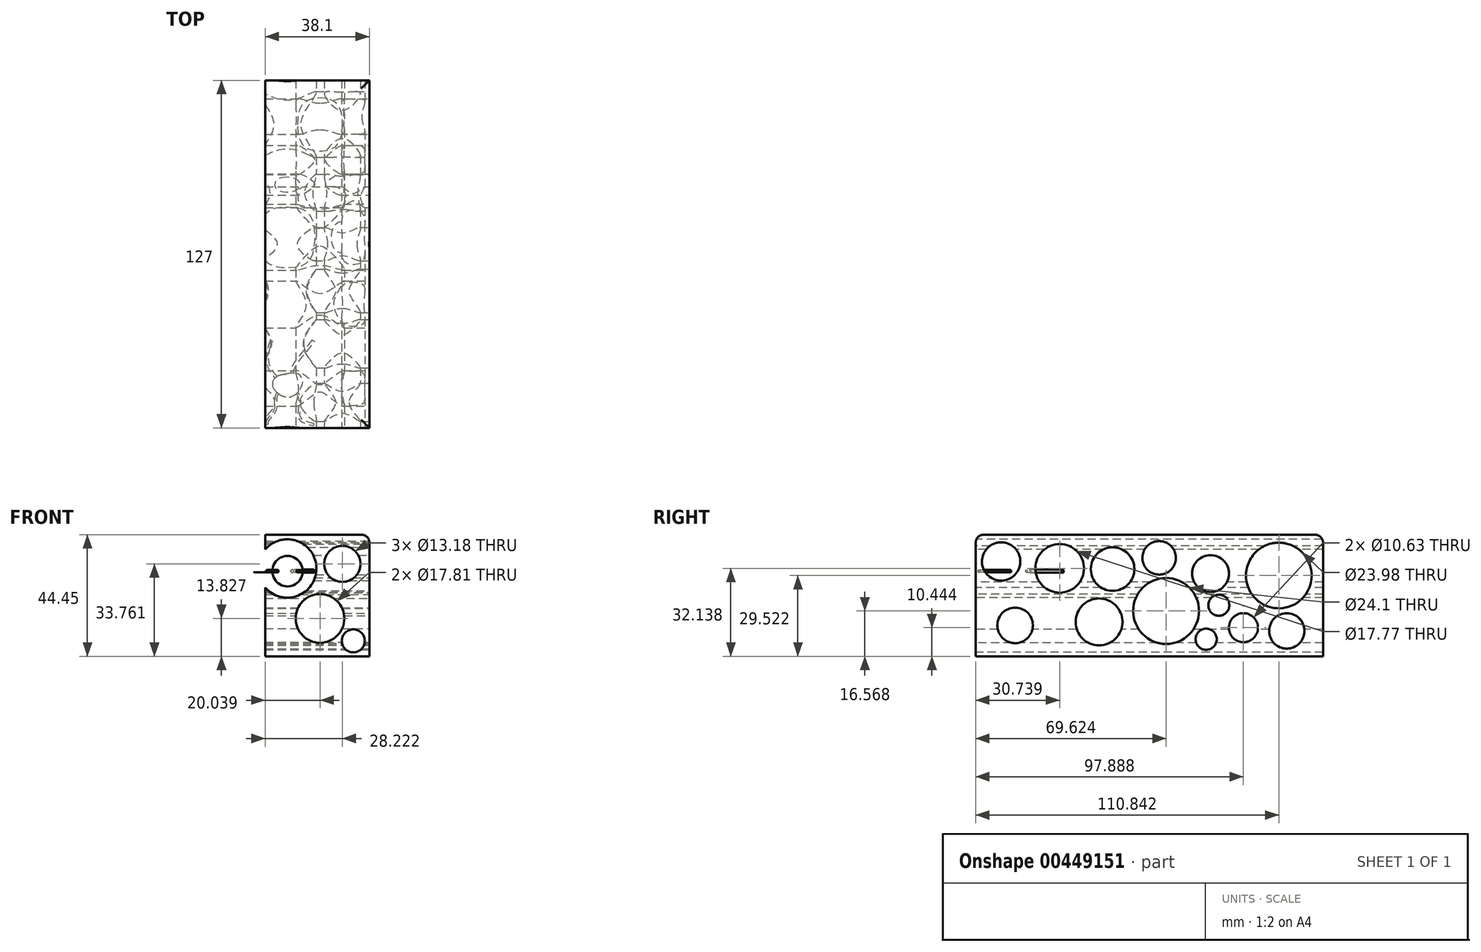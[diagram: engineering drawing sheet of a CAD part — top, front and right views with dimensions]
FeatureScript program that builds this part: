
annotation { "Feature Type Name" : "Feature", "Feature Type Description" : "" }
export const myFeature = defineFeature(function(context is Context, id is Id, definition is map)
    precondition{}
    {
        {
            var Q0;
            Q0=qCreatedBy(makeId("Front.planeOp"),FACE);
            var sketch = newSketch(context, id + "F0", { "sketchPlane" : qUnion([Q0])});
            skLineSegment(sketch, "E0.bottom", {"start": v(-47.65, 23.5) * mm, "end": v(53.95, 23.5) * mm});
            skLineSegment(sketch, "E0.top", {"start": v(-47.65, -20.95) * mm, "end": v(53.95, -20.95) * mm});
            skLineSegment(sketch, "E0.left", {"start": v(-47.65, 23.5) * mm, "end": v(-47.65, -20.95) * mm});
            skLineSegment(sketch, "E0.right", {"start": v(53.95, 23.5) * mm, "end": v(53.95, -20.95) * mm});
            skSolve(sketch);
        }
        {
            var Q0;
            Q0=qSketchRegion(id+"F0",true);
            extrude(context, id + "F1", {"entities" : qUnion([Q0]), "endBound" : BoundingType.SYMMETRIC, "depth" : 127 * mm});
        }
        {
            var Q0;
            Q0=makeQuery(id+"F1.opExtrude","SWEPT_FACE",FACE,{"disambiguationData":[OSD([sQuery(id+"F0.wireOp",EDGE,"E0.right")])]});
            var sketch = newSketch(context, id + "F2", { "sketchPlane" : qUnion([Q0])});
            skCircle(sketch, "E1", {"center": v(-13.43, 10.93) * mm, "radius": 7.97 * mm});
            skCircle(sketch, "E2", {"center": v(6.12, -4.38) * mm, "radius": 12.05 * mm});
            skCircle(sketch, "E3", {"center": v(47.34, 8.57) * mm, "radius": 12 * mm});
            skCircle(sketch, "E4", {"center": v(34.39, -10.5) * mm, "radius": 5.31 * mm});
            skCircle(sketch, "E5", {"center": v(-32.76, 11.19) * mm, "radius": 8.88 * mm});
            skCircle(sketch, "E6", {"center": v(-18.37, -8.39) * mm, "radius": 8.57 * mm});
            skCircle(sketch, "E7", {"center": v(3.6, 15.02) * mm, "radius": 6.12 * mm});
            skCircle(sketch, "E8", {"center": v(22.38, 9.28) * mm, "radius": 6.74 * mm});
            skCircle(sketch, "E9", {"center": v(-49.06, -9.65) * mm, "radius": 6.5 * mm});
            skCircle(sketch, "E10", {"center": v(-54.17, 13.7) * mm, "radius": 7.01 * mm});
            skCircle(sketch, "E11", {"center": v(50.25, -11.68) * mm, "radius": 6.46 * mm});
            skCircle(sketch, "E12", {"center": v(20.78, -14.72) * mm, "radius": 3.87 * mm});
            skCircle(sketch, "E13", {"center": v(25.4, -2.3) * mm, "radius": 3.85 * mm});
            skSolve(sketch);
        }
        {
            var Q0;
            Q0=qSketchRegion(id+"F2",true);
            extrude(context, id + "F3", {"entities" : qUnion([Q0]), "operationType" : NewBodyOperationType.REMOVE, "endBound" : BoundingType.THROUGH_ALL, "oppositeDirection" : true, "depth" : 25.4 * mm});
        }
        {
            var Q0;
            Q0=makeQuery(id+"F1.opExtrude","CAP_FACE",FACE,{"disambiguationData":[OSD([sQuery(id+"F0.wireOp",EDGE,"E0.bottom"),sQuery(id+"F0.wireOp",EDGE,"E0.top"),sQuery(id+"F0.wireOp",EDGE,"E0.left"),sQuery(id+"F0.wireOp",EDGE,"E0.right")])],"isStart":false});
            var sketch = newSketch(context, id + "F4", { "sketchPlane" : qUnion([Q0])});
            skCircle(sketch, "E14", {"center": v(-37.55, 12.4) * mm, "radius": 8.73 * mm});
            skCircle(sketch, "E15", {"center": v(-15.94, 7.15) * mm, "radius": 11.37 * mm});
            skCircle(sketch, "E16", {"center": v(-35.46, -10.9) * mm, "radius": 9.74 * mm});
            skCircle(sketch, "E17", {"center": v(-16.15, -8.8) * mm, "radius": 3.78 * mm});
            skCircle(sketch, "E18", {"center": v(-3.56, -12.79) * mm, "radius": 7.5 * mm});
            skCircle(sketch, "E19", {"center": v(23.93, 11.13) * mm, "radius": 10.66 * mm});
            skCircle(sketch, "E20", {"center": v(35.89, -7.12) * mm, "radius": 8.9 * mm});
            skCircle(sketch, "E21", {"center": v(44.07, 12.81) * mm, "radius": 6.59 * mm});
            skCircle(sketch, "E22", {"center": v(48.06, -15.3) * mm, "radius": 4.2 * mm});
            skSolve(sketch);
        }
        {
            var Q0;
            Q0=qSketchRegion(id+"F4",true);
            extrude(context, id + "F5", {"entities" : qUnion([Q0]), "operationType" : NewBodyOperationType.REMOVE, "endBound" : BoundingType.THROUGH_ALL, "oppositeDirection" : true, "depth" : 25.4 * mm});
        }
        {
            var Q0;
            Q0=makeQuery(id+"F1.opExtrude","SWEPT_FACE",FACE,{"disambiguationData":[OSD([sQuery(id+"F0.wireOp",EDGE,"E0.left")])]});
            extrude(context, id + "F6", {"entities" : qUnion([Q0]), "operationType" : NewBodyOperationType.REMOVE, "oppositeDirection" : true, "depth" : 63.5 * mm});
        }
        {
            var Q0;
            Q0=qCreatedBy(makeId("Top.planeOp"),FACE);
            cPlane(context, id + "F7", {"entities" : qUnion([Q0]), "cplaneType" : CPlaneType.OFFSET, "offset" : 10.16 * mm, "width" : 152.4 * mm, "height" : 152.4 * mm});
        }
        {
            var Q0;
            Q0=qCreatedBy(id+"F7.planeOp",FACE);
            var sketch = newSketch(context, id + "F8", { "sketchPlane" : qUnion([Q0])});
            skLineSegment(sketch, "E23", {"start": v(23.44, -44) * mm, "end": v(24.96, -52.2) * mm});
            skFitSpline(sketch, "E24", {"points": [v(23.44, -44) * mm, v(18.9, -45.89) * mm, v(18.69, -48.64) * mm, v(20.22, -50.6) * mm, v(24.96, -52.2) * mm], "startDerivative": vector(-23.34, 0) * mm, "endDerivative": vector(30.2, 0) * mm});
            skSolve(sketch);
        }
        {
            var Q0;
            Q0 = qSketchRegion(id + "F8", true);
            var Q1;
            Q1=sQuery(id+"F8.wireOp",EDGE,"E23");
            revolve(context, id + "F9", {"entities" : qUnion([Q0]), "axis" : qUnion([Q1]), "revolveType" : RevolveType.FULL});
        }
        {
            var Q0;
            Q0=qCreatedBy(id+"F7.planeOp",FACE);
            var sketch = newSketch(context, id + "F10", { "sketchPlane" : qUnion([Q0])});
            skFitSpline(sketch, "E25", {"points": [v(27.4, -50.6) * mm, v(28.38, -59.67) * mm, v(33.53, -62.33) * mm], "startDerivative": vector(12.8, -14.53) * mm, "endDerivative": vector(13.56, -3.44) * mm});
            skFitSpline(sketch, "E26", {"points": [v(20.63, -50.52) * mm, v(19.37, -57.33) * mm, v(16.6, -62.22) * mm], "startDerivative": vector(-8.86, -10.73) * mm, "endDerivative": vector(2.94, -12.7) * mm});
            skFitSpline(sketch, "E27", {"points": [v(20.06, -45.17) * mm, v(17.1, -40.67) * mm, v(18.2, -31.72) * mm], "startDerivative": vector(-8.93, 9.06) * mm, "endDerivative": vector(8.78, 17.46) * mm});
            skFitSpline(sketch, "E28", {"points": [v(25.8, -43.54) * mm, v(33.43, -31.62) * mm], "startDerivative": vector(-1.85, 9.77) * mm, "endDerivative": vector(7.6, 11.76) * mm});
            skSolve(sketch);
        }
        {
            var Q0;
            Q0=sQuery(id+"F10.wireOp",EDGE,"E27");
            var Q1;
            Q1=sQuery(id+"F10.wireOp",VERTEX,"E27.end");
            cPlane(context, id + "F11", {"entities" : qUnion([Q0, Q1]), "cplaneType" : CPlaneType.CURVE_POINT, "offset" : 25.4 * mm, "width" : 152.4 * mm, "height" : 152.4 * mm});
        }
        {
            var Q0;
            Q0=qCreatedBy(id+"F11.planeOp",FACE);
            var sketch = newSketch(context, id + "F12", { "sketchPlane" : qUnion([Q0])});
            skCircle(sketch, "E29", {"center": v(-30.5, 10.16) * mm, "radius": 0.46 * mm});
            skSolve(sketch);
        }
        {
            var Q0;
            Q0=makeQuery(id+"F12.imprint","IMPRINT",FACE,{"disambiguationData":[TD([[makeQuery(id+"F12.imprint","IMPRINT",EDGE,{"derivedFrom":sQuery(id+"F12.wireOp",EDGE,"E29")}),1.0]])]});
            var Q1;
            Q1=sQuery(id+"F10.wireOp",EDGE,"E27");
            sweep(context, id + "F13", {"operationType" : NewBodyOperationType.ADD, "profiles" : qUnion([Q0]), "path" : qUnion([Q1])});
        }
        {
            var Q0;
            Q0=sQuery(id+"F10.wireOp",EDGE,"E28");
            var Q1;
            Q1=sQuery(id+"F10.wireOp",VERTEX,"E28.end");
            cPlane(context, id + "F14", {"entities" : qUnion([Q0, Q1]), "cplaneType" : CPlaneType.CURVE_POINT, "offset" : 25.4 * mm, "width" : 152.4 * mm, "height" : 152.4 * mm});
        }
        {
            var Q0;
            Q0=qCreatedBy(id+"F14.planeOp",FACE);
            var sketch = newSketch(context, id + "F15", { "sketchPlane" : qUnion([Q0])});
            skCircle(sketch, "E30", {"center": v(-45.24, 10.16) * mm, "radius": 0.56 * mm});
            skSolve(sketch);
        }
        {
            var Q0;
            Q0=makeQuery(id+"F15.imprint","IMPRINT",FACE,{"disambiguationData":[TD([[makeQuery(id+"F15.imprint","IMPRINT",EDGE,{"derivedFrom":sQuery(id+"F15.wireOp",EDGE,"E30")}),1.0]])]});
            var Q1;
            Q1=sQuery(id+"F10.wireOp",EDGE,"E28");
            sweep(context, id + "F16", {"operationType" : NewBodyOperationType.ADD, "profiles" : qUnion([Q0]), "path" : qUnion([Q1])});
        }
        {
            var Q0;
            Q0=sQuery(id+"F10.wireOp",EDGE,"E26");
            var Q1;
            Q1=sQuery(id+"F10.wireOp",VERTEX,"E26.end");
            cPlane(context, id + "F17", {"entities" : qUnion([Q0, Q1]), "cplaneType" : CPlaneType.CURVE_POINT, "offset" : 25.4 * mm, "width" : 152.4 * mm, "height" : 152.4 * mm});
        }
        {
            var Q0;
            Q0=qCreatedBy(id+"F17.planeOp",FACE);
            var sketch = newSketch(context, id + "F18", { "sketchPlane" : qUnion([Q0])});
            skCircle(sketch, "E31", {"center": v(2.16, 10.16) * mm, "radius": 0.42 * mm});
            skSolve(sketch);
        }
        {
            var Q0;
            Q0=makeQuery(id+"F18.imprint","IMPRINT",FACE,{"disambiguationData":[TD([[makeQuery(id+"F18.imprint","IMPRINT",EDGE,{"derivedFrom":sQuery(id+"F18.wireOp",EDGE,"E31")}),1.0]])]});
            var Q1;
            Q1=sQuery(id+"F10.wireOp",EDGE,"E26");
            sweep(context, id + "F19", {"operationType" : NewBodyOperationType.ADD, "profiles" : qUnion([Q0]), "path" : qUnion([Q1])});
        }
        {
            var Q0;
            Q0=sQuery(id+"F10.wireOp",EDGE,"E25");
            var Q1;
            Q1=sQuery(id+"F10.wireOp",VERTEX,"E25.2.internal");
            cPlane(context, id + "F20", {"entities" : qUnion([Q0, Q1]), "cplaneType" : CPlaneType.CURVE_POINT, "offset" : 25.4 * mm, "width" : 152.4 * mm, "height" : 152.4 * mm});
        }
        {
            var Q0;
            Q0=qCreatedBy(id+"F20.planeOp",FACE);
            var sketch = newSketch(context, id + "F21", { "sketchPlane" : qUnion([Q0])});
            skCircle(sketch, "E32", {"center": v(-52.2, 10.16) * mm, "radius": 0.4 * mm});
            skSolve(sketch);
        }
        {
            var Q0;
            Q0=makeQuery(id+"F21.imprint","IMPRINT",FACE,{"disambiguationData":[TD([[makeQuery(id+"F21.imprint","IMPRINT",EDGE,{"derivedFrom":sQuery(id+"F21.wireOp",EDGE,"E32")}),1.0]])]});
            var Q1;
            Q1=sQuery(id+"F10.wireOp",EDGE,"E25");
            sweep(context, id + "F22", {"operationType" : NewBodyOperationType.ADD, "profiles" : qUnion([Q0]), "path" : qUnion([Q1])});
        }
        {
            var Q0;
            Q0=makeQuery(id+"F1.opExtrude","SWEPT_EDGE",EDGE,{"disambiguationData":[OSD([sQuery(id+"F0.wireOp",EDGE,"E0.bottom"),sQuery(id+"F0.wireOp",EDGE,"E0.right")])]});
            var Q1;
            Q1=makeQuery(id+"F1.opExtrude","CAP_EDGE",EDGE,{"disambiguationData":[OSD([sQuery(id+"F0.wireOp",EDGE,"E0.bottom")])],"isStart":false});
            var Q2;
            Q2=makeQuery(id+"F6.boolean.opBoolean","COPY",EDGE,{"derivedFrom":makeQuery(id+"F6.opExtrude","CAP_EDGE",EDGE,{"disambiguationData":[OSD([sQuery(id+"F0.wireOp",EDGE,"E0.bottom"),sQuery(id+"F0.wireOp",EDGE,"E0.left")])],"isStart":false})});
            var Q3;
            Q3=makeQuery(id+"F1.opExtrude","CAP_EDGE",EDGE,{"disambiguationData":[OSD([sQuery(id+"F0.wireOp",EDGE,"E0.bottom")])],"isStart":true});
            fillet(context, id + "F23", {"entities" : qUnion([Q0, Q1, Q2, Q3]), "radius" : 3 * mm, "tangentPropagation" : true, "allowEdgeOverflow" : false});
        }
    });
